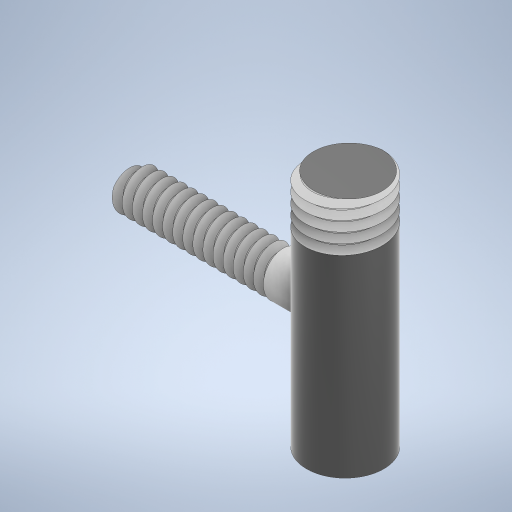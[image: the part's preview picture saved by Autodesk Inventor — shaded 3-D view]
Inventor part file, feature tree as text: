
AUTODESK INVENTOR PART (.ipt)
format: ipt  version: 2024 (Build 280153000, 153)  size: 573,952 bytes
history: native  units: mm
features: sketch x4, extrude x2, helix x2, plane x1
ambient origin geometry x8: Origin, YZ Plane, XZ Plane, XY Plane, X Axis, Y Axis, Z Axis, Center Point
bodies: Solid1 (feature_tree)
feature tree (9):
  extrude  "Extrusion1"  Depth=40.0mm TaperAngle=0.0deg
  plane  "Work Plane1"
  extrude  "Extrusion3"  Depth=1.7mm TaperAngle=0.0deg
  helix  "Coil1"  [1 undecoded]
  helix  "Coil2"  [1 undecoded]
  sketch  "Sketch1"  dims[d0=13.0mm d1=40.0mm d2=0.0mm]
  sketch  "Sketch4"  dims[d9=7.0mm d10=40.0mm d11=0.0mm d12=2.0mm d13=1.7mm]
  sketch  "Sketch5"  dims[d14=60.0deg]
  sketch  "Sketch6"  dims[d15=0.2mm d16=1.7mm d17=28.0mm d18=10.0mm d19=0.0mm d20=90.0deg d21=90.0deg d22=0.0mm d23=0.0mm d24=1.7mm d25=60.0deg d26=0.2mm d27=1.7mm d28=15.0mm d29=10.0mm d30=0.0mm d31=90.0deg d32=90.0deg d33=0.0mm d34=0.0mm]
note: 2 required parameter values undecoded (feature->parameter linkage not recoverable at this tier; creation-order binding heuristic only, values carry confidence <= 0.55)
